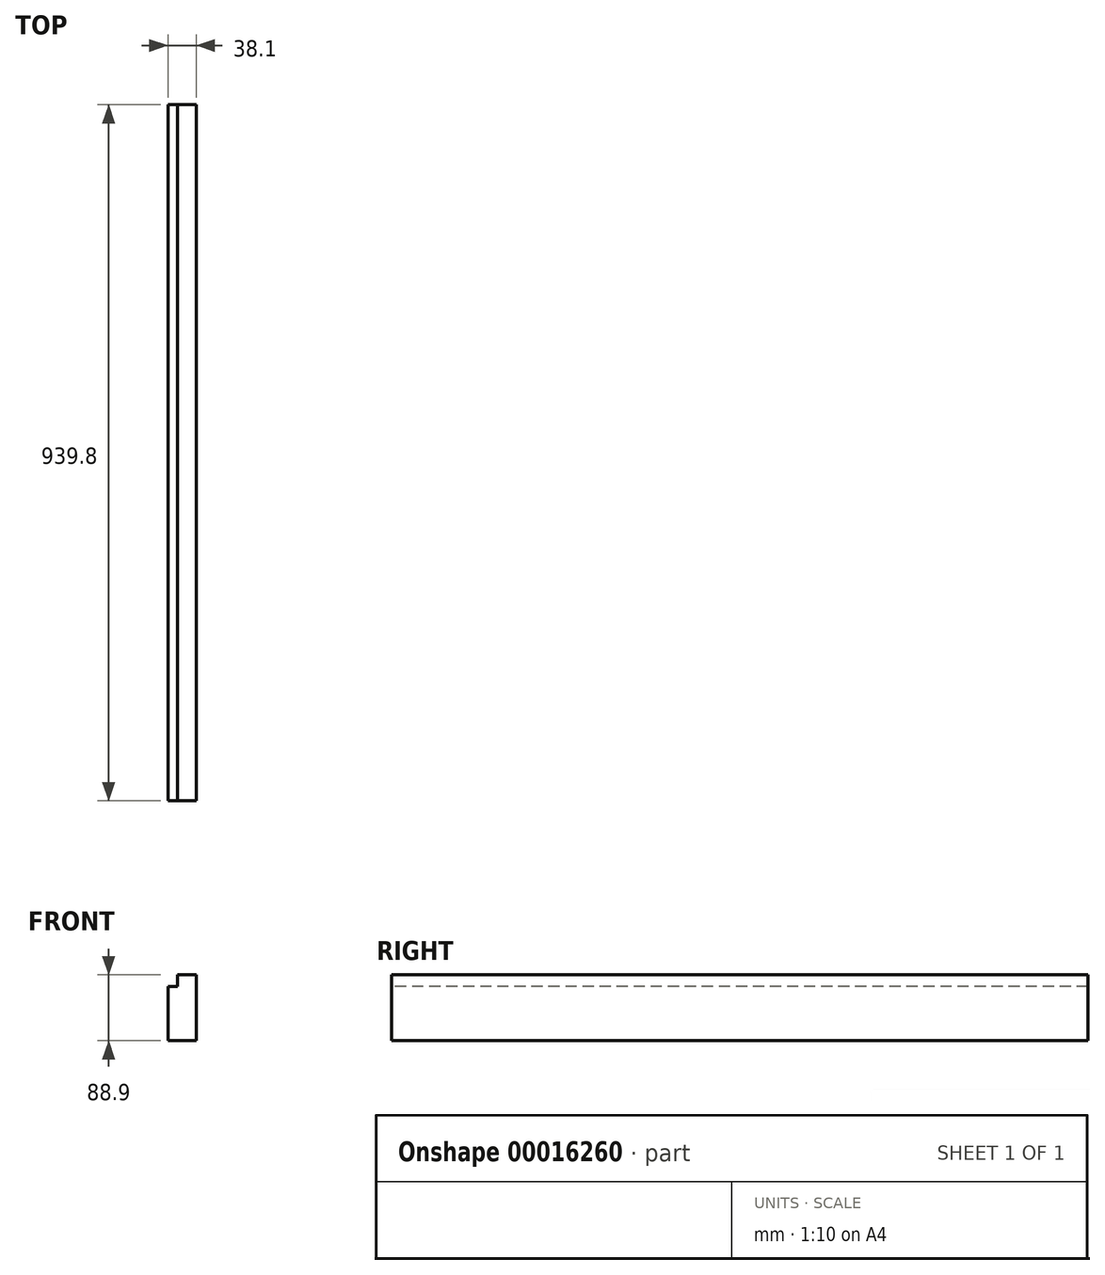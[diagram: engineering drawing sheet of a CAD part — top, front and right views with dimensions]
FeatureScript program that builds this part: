
annotation { "Feature Type Name" : "Feature", "Feature Type Description" : "" }
export const myFeature = defineFeature(function(context is Context, id is Id, definition is map)
    precondition{}
    {
        {
            var Q0;
            Q0=qCreatedBy(makeId("Front.planeOp"),FACE);
            var sketch = newSketch(context, id + "F0", { "sketchPlane" : qUnion([Q0])});
            skLineSegment(sketch, "E0.bottom", {"start": v(0, 0) * mm, "end": v(-38.1, 0) * mm});
            skLineSegment(sketch, "E0.left", {"start": v(0, 0) * mm, "end": v(0, 88.9) * mm});
            skLineSegment(sketch, "E0.right", {"start": v(-38.1, 0) * mm, "end": v(-38.1, 73.03) * mm});
            skLineSegment(sketch, "E1.top", {"start": v(0, 88.9) * mm, "end": v(-25.4, 88.9) * mm});
            skLineSegment(sketch, "E1.right", {"start": v(-25.4, 73.03) * mm, "end": v(-25.4, 88.9) * mm});
            skLineSegment(sketch, "E2", {"start": v(-38.1, 73.03) * mm, "end": v(-25.4, 73.03) * mm});
            skSolve(sketch);
        }
        {
            var Q0;
            Q0=makeQuery(id+"F0.imprint","IMPRINT",FACE,{"disambiguationData":[TD([[makeQuery(id+"F0.imprint","IMPRINT",EDGE,{"derivedFrom":sQuery(id+"F0.wireOp",EDGE,"E0.bottom")}),-1.0]])]});
            extrude(context, id + "F1", {"entities" : qUnion([Q0]), "oppositeDirection" : true, "depth" : 939.8 * mm});
        }
    });
